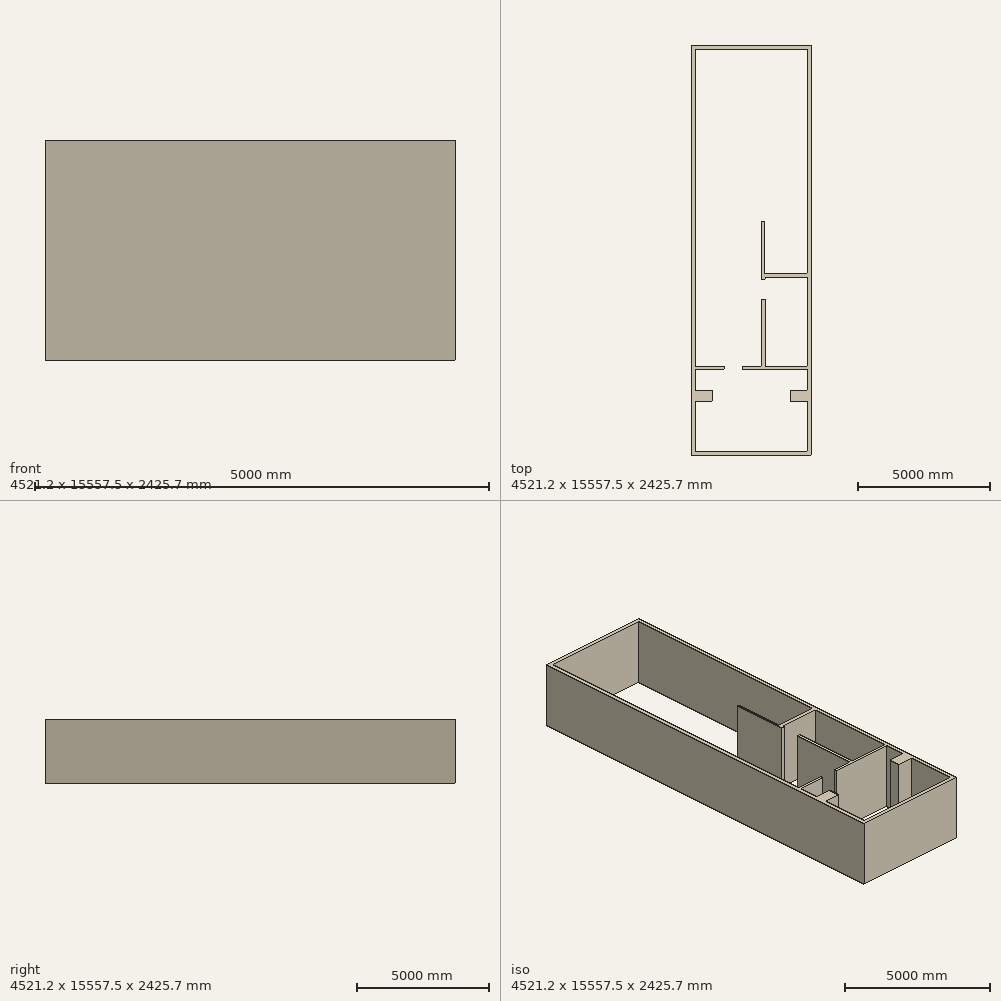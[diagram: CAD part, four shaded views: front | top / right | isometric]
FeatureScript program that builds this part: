
annotation { "Feature Type Name" : "Feature", "Feature Type Description" : "" }
export const myFeature = defineFeature(function(context is Context, id is Id, definition is map)
    precondition{}
    {
        {
            var Q0;
            Q0=qCreatedBy(makeId("Top.planeOp"),FACE);
            cPlane(context, id + "F0", {"entities" : qUnion([Q0]), "cplaneType" : CPlaneType.OFFSET, "offset" : 406.4 * mm, "oppositeDirection" : true, "width" : 152.4 * mm, "height" : 152.4 * mm});
        }
        {
            var Q0;
            Q0=qCreatedBy(id+"F0.planeOp",FACE);
            var sketch = newSketch(context, id + "F1", { "sketchPlane" : qUnion([Q0])});
            skLineSegment(sketch, "E0.bottom", {"start": v(0, 0) * mm, "end": v(635, 0) * mm});
            skLineSegment(sketch, "E0.top", {"start": v(0, 12941.3) * mm, "end": v(4216.4, 12941.3) * mm});
            skLineSegment(sketch, "E0.left", {"start": v(0, 0) * mm, "end": v(0, 800.1) * mm});
            skLineSegment(sketch, "E0.right", {"start": v(4216.4, 0) * mm, "end": v(4216.4, 800.1) * mm});
            skLineSegment(sketch, "E1.0", {"start": v(-152.4, -2463.8) * mm, "end": v(-152.4, 13093.7) * mm});
            skLineSegment(sketch, "E1.2", {"start": v(4368.8, -2463.8) * mm, "end": v(4368.8, 13093.7) * mm});
            skLineSegment(sketch, "E1.3", {"start": v(-152.4, 13093.7) * mm, "end": v(4368.8, 13093.7) * mm});
            skLineSegment(sketch, "E2.top", {"start": v(2501.9, 3467.1) * mm, "end": v(2628.9, 3467.1) * mm});
            skLineSegment(sketch, "E2.left", {"start": v(2501.9, 901.7) * mm, "end": v(2501.9, 3467.1) * mm});
            skLineSegment(sketch, "E2.right", {"start": v(2628.9, 901.7) * mm, "end": v(2628.9, 3467.1) * mm});
            skLineSegment(sketch, "E3.trimOffspring", {"start": v(3581.4, 0) * mm, "end": v(4216.4, 0) * mm});
            skLineSegment(sketch, "E4.bottom", {"start": v(2501.9, 4229.1) * mm, "end": v(2628.9, 4229.1) * mm});
            skLineSegment(sketch, "E4.left", {"start": v(2501.9, 4229.1) * mm, "end": v(2501.9, 6400.8) * mm});
            skLineSegment(sketch, "E5.bottom", {"start": v(2501.9, 6400.8) * mm, "end": v(2590.8, 6400.8) * mm});
            skLineSegment(sketch, "E6", {"start": v(2628.9, 4305.3) * mm, "end": v(4216.4, 4305.3) * mm});
            skLineSegment(sketch, "E7.0", {"start": v(2590.8, 4432.3) * mm, "end": v(4216.4, 4432.3) * mm});
            skLineSegment(sketch, "E8.trimOffspring", {"start": v(2590.8, 4432.3) * mm, "end": v(2590.8, 6400.8) * mm});
            skLineSegment(sketch, "E9", {"start": v(2628.9, 4305.3) * mm, "end": v(2628.9, 4229.1) * mm});
            skLineSegment(sketch, "E10.trimOffspring", {"start": v(4216.4, 4432.3) * mm, "end": v(4216.4, 12941.3) * mm});
            skLineSegment(sketch, "E11", {"start": v(635, 0) * mm, "end": v(635, -431.8) * mm});
            skLineSegment(sketch, "E12", {"start": v(635, -431.8) * mm, "end": v(0, -431.8) * mm});
            skLineSegment(sketch, "E13", {"start": v(0, -431.8) * mm, "end": v(0, -2311.4) * mm});
            skLineSegment(sketch, "E14", {"start": v(0, -2311.4) * mm, "end": v(4216.4, -2311.4) * mm});
            skLineSegment(sketch, "E15", {"start": v(4216.4, -2311.4) * mm, "end": v(4216.4, -431.8) * mm});
            skLineSegment(sketch, "E16", {"start": v(4216.4, -431.8) * mm, "end": v(3581.4, -431.8) * mm});
            skLineSegment(sketch, "E17", {"start": v(3581.4, -431.8) * mm, "end": v(3581.4, 0) * mm});
            skLineSegment(sketch, "E18", {"start": v(-152.4, -2463.8) * mm, "end": v(4368.8, -2463.8) * mm});
            skLineSegment(sketch, "E19.bottom", {"start": v(0, 4381.5) * mm, "end": v(838.2, 4381.5) * mm, "construction": true});
            skLineSegment(sketch, "E19.top", {"start": v(0, 1765.3) * mm, "end": v(838.2, 1765.3) * mm, "construction": true});
            skLineSegment(sketch, "E19.left", {"start": v(0, 4381.5) * mm, "end": v(0, 1765.3) * mm, "construction": true});
            skLineSegment(sketch, "E19.right", {"start": v(838.2, 4381.5) * mm, "end": v(838.2, 1765.3) * mm, "construction": true});
            skLineSegment(sketch, "E20", {"start": v(0, 800.1) * mm, "end": v(1079.5, 800.1) * mm});
            skLineSegment(sketch, "E21", {"start": v(1079.5, 800.1) * mm, "end": v(1079.5, 901.7) * mm});
            skLineSegment(sketch, "E22", {"start": v(1079.5, 901.7) * mm, "end": v(0, 901.7) * mm});
            skLineSegment(sketch, "E23.trimOffspring", {"start": v(0, 901.7) * mm, "end": v(0, 12941.3) * mm});
            skLineSegment(sketch, "E24", {"start": v(4216.4, 800.1) * mm, "end": v(1778, 800.1) * mm});
            skLineSegment(sketch, "E25", {"start": v(1778, 800.1) * mm, "end": v(1778, 901.7) * mm});
            skLineSegment(sketch, "E26", {"start": v(1778, 901.7) * mm, "end": v(2501.9, 901.7) * mm});
            skLineSegment(sketch, "E27.trimOffspring", {"start": v(2628.9, 901.7) * mm, "end": v(4216.4, 901.7) * mm});
            skLineSegment(sketch, "E28.trimOffspring", {"start": v(4216.4, 901.7) * mm, "end": v(4216.4, 4305.3) * mm});
            skSolve(sketch);
        }
        {
            var Q0;
            Q0 = qSketchRegion(id + "F1", true);
            var Q1;
            Q1=makeQuery(id+"F1.imprint","IMPRINT",FACE,{"disambiguationData":[TD([[makeQuery(id+"F1.imprint","IMPRINT",EDGE,{"derivedFrom":sQuery(id+"F1.wireOp",EDGE,"F7Un9YJU-Cci4-44Dg-9Xuj-NicAz26EByOO.bottom")}),-1.0]])]});
            extrude(context, id + "F2", {"entities" : qUnion([Q0, Q1]), "oppositeDirection" : true, "depth" : 2425.7 * mm});
        }
    });
